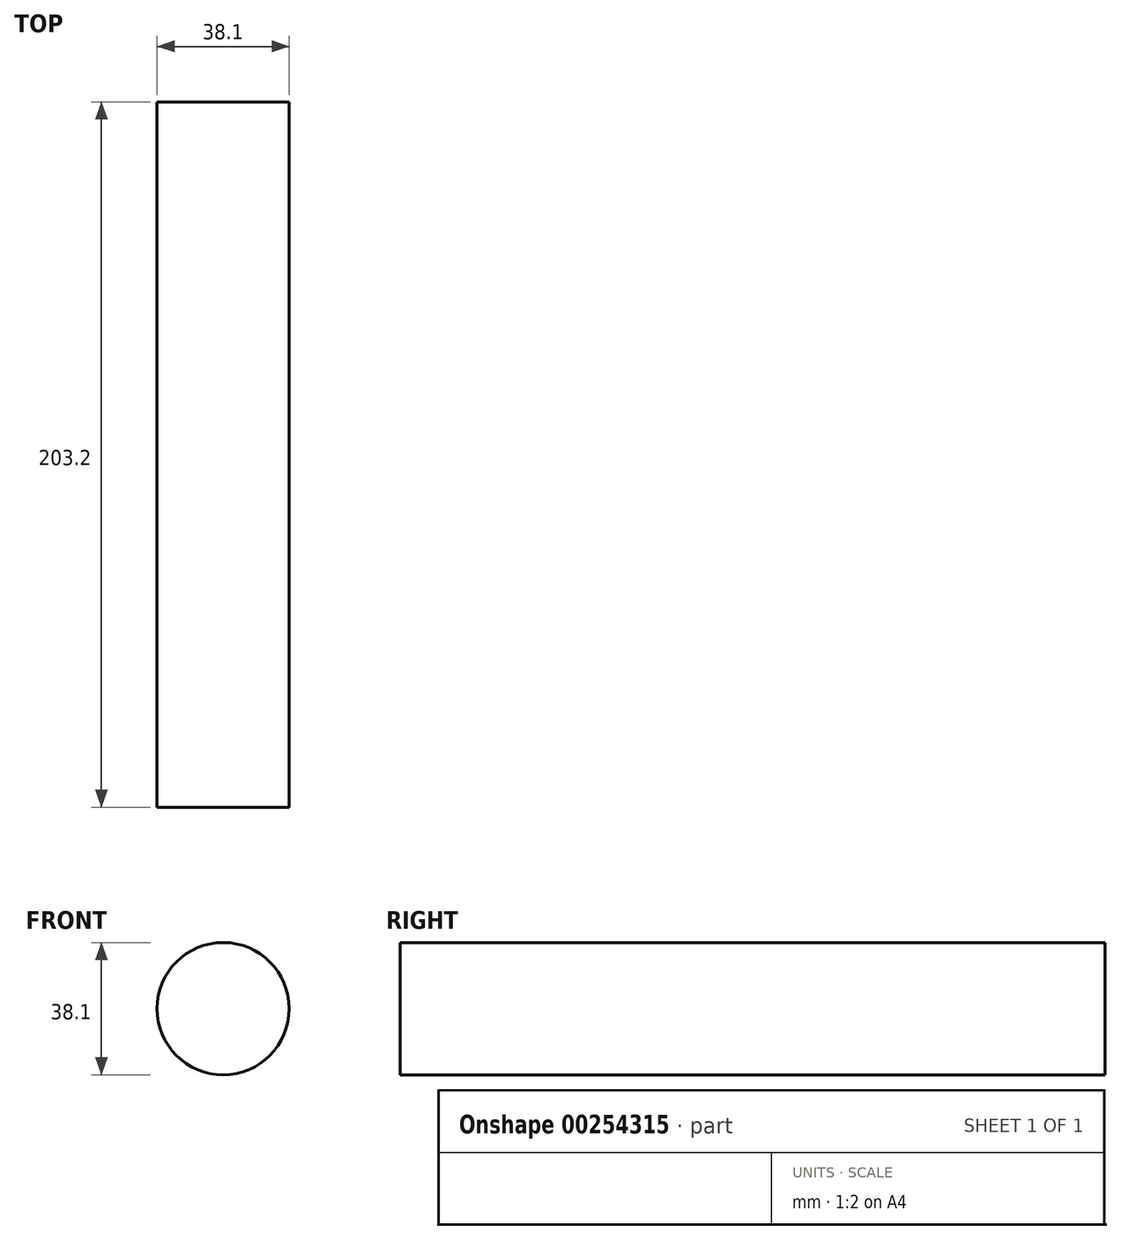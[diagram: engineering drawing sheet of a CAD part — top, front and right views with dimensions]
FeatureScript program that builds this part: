
annotation { "Feature Type Name" : "Feature", "Feature Type Description" : "" }
export const myFeature = defineFeature(function(context is Context, id is Id, definition is map)
    precondition{}
    {
        {
            var Q0;
            Q0=qCreatedBy(makeId("Front.planeOp"),FACE);
            var sketch = newSketch(context, id + "F0", { "sketchPlane" : qUnion([Q0])});
            skCircle(sketch, "E0", {"center": v(0, 0) * mm, "radius": 38.1 * mm});
            skCircle(sketch, "E1", {"center": v(0, 0) * mm, "radius": 19.05 * mm});
            skSolve(sketch);
        }
        {
            var Q0;
            Q0=makeQuery(id+"F0.imprint","IMPRINT",FACE,{"disambiguationData":[TD([[makeQuery(id+"F0.imprint","IMPRINT",EDGE,{"derivedFrom":sQuery(id+"F0.wireOp",EDGE,"E1")}),1.0]])]});
            extrude(context, id + "F1", {"entities" : qUnion([Q0]), "endBound" : BoundingType.SYMMETRIC, "depth" : 101.6 * mm});
        }
        {
            var Q0;
            Q0=makeQuery(id+"F1.opExtrude","CAP_FACE",FACE,{"disambiguationData":[OSD([sQuery(id+"F0.wireOp",EDGE,"E1")])],"isStart":false});
            extrude(context, id + "F2", {"entities" : qUnion([Q0]), "operationType" : NewBodyOperationType.ADD, "depth" : 50.8 * mm});
        }
        {
            var Q0;
            Q0=makeQuery(id+"F1.opExtrude","CAP_FACE",FACE,{"disambiguationData":[OSD([sQuery(id+"F0.wireOp",EDGE,"E1")])],"isStart":true});
            extrude(context, id + "F3", {"entities" : qUnion([Q0]), "operationType" : NewBodyOperationType.ADD, "depth" : 50.8 * mm});
        }
    });
